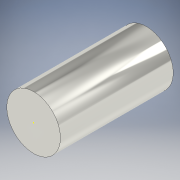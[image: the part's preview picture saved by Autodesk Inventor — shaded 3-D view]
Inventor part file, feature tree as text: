
AUTODESK INVENTOR PART (.ipt)
format: ipt  version: 2021 (Build 250183000, 183)  size: 107,008 bytes
history: native  units: mm
features: sketch x3, extrude x1
ambient origin geometry x8: Origin, YZ Plane, XZ Plane, XY Plane, X Axis, Y Axis, Z Axis, Center Point
bodies: Solid1 (feature_tree)
feature tree (4):
  extrude  "Extrusion1"  Depth=25.4mm TaperAngle=0.0deg
  sketch  "Sketch2"
  sketch  "Sketch3"
  sketch  "Sketch1"  dims[d0=12.082mm d1=25.4mm d2=0.0mm]
